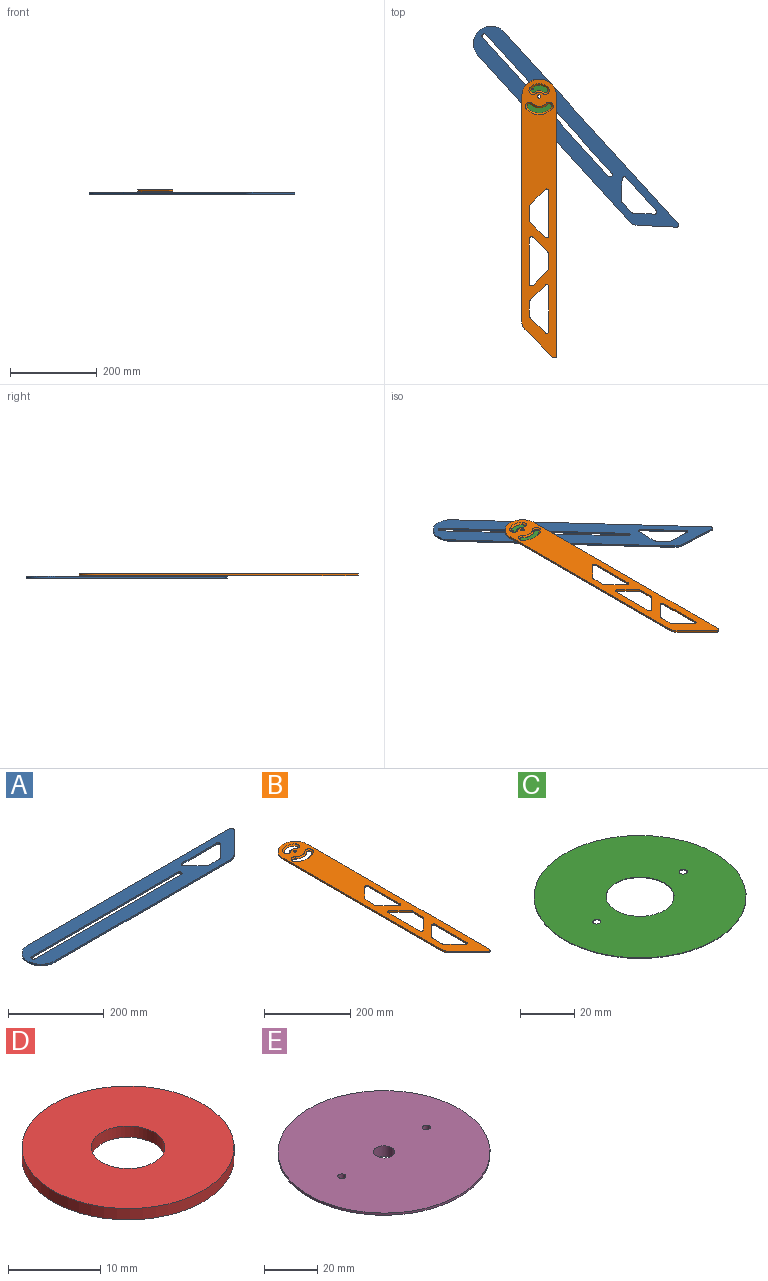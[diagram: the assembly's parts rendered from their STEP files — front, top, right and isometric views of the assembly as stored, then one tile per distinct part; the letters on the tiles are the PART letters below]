
ASSEMBLY  parts=5 mates=4
PART A: 20 faces, bbox 642.5x80x4 mm
  f0: plane 33.54x33.54mm, normal (0.71,0.71,0), area 189.7mm2, adj f14,f15,f16,f19
  f1: plane 28.72x4mm, normal (0,1,0), area 114.9mm2, adj f14,f15,f16,f17
  f2: plane 33.54x33.54mm, normal (-0.71,0.71,0), area 189.7mm2, adj f14,f15,f17,f18
  f3: cylinder r=5.25mm len=10.5mm, axis (0,0,1), area 66mm2, adj f4,f11,f14,f15
  f4: plane 431.4x4mm, normal (0,-1,0), area 1725.6mm2, adj f3,f5,f14,f15
  f5: cylinder r=5.25mm len=10.5mm, axis (0,0,1), area 66mm2, adj f4,f11,f14,f15
  f6: cylinder r=40mm len=80mm, axis (0,0,1), area 502.7mm2, adj f7,f12,f14,f15
  f7: plane 597.53x4mm, normal (0,1,0), area 2390.1mm2, adj f6,f8,f14,f15
  f8: cylinder r=5mm len=8.54mm, axis (0,0,1), area 47.1mm2, adj f7,f9,f14,f15
  f9: plane 64.14x64.14mm, normal (0.71,-0.71,0), area 362.8mm2, adj f8,f10,f14,f15
  f10: cylinder r=25mm len=17.68mm, axis (0,0,1), area 78.5mm2, adj f9,f12,f14,f15
  f11: plane 431.4x4mm, normal (0,1,0), area 1725.6mm2, adj f3,f5,f14,f15
  f12: plane 519.24x4mm, normal (0,-1,0), area 2077mm2, adj f6,f10,f14,f15
  f13: plane 102.86x4mm, normal (0,-1,0), area 411.4mm2, adj f14,f15,f18,f19
  f14: plane 642.53x80mm, normal (0,0,-1), area 39796.7mm2, adj f0,f1,f2,f3,f4,f5,f6,f7
  f15: plane 642.53x80mm, normal (0,0,1), area 39796.7mm2, adj f0,f1,f2,f3,f4,f5,f6,f7
  f16: cylinder r=10mm len=7.07mm, axis (0,0,-1), area 31.4mm2, adj f0,f1,f14,f15
  f17: cylinder r=10mm len=7.07mm, axis (0,0,-1), area 31.4mm2, adj f1,f2,f14,f15
  f18: cylinder r=5mm len=8.54mm, axis (0,0,-1), area 47.1mm2, adj f2,f13,f14,f15
  f19: cylinder r=5mm len=8.54mm, axis (0,0,-1), area 47.1mm2, adj f0,f13,f14,f15
PART B: 49 faces, bbox 80x642.5x4 mm
  f0: plane 102.86x4mm, normal (-1,0,0), area 411.4mm2, adj f19,f20,f47,f48
  f1: plane 33.54x33.54mm, normal (0.71,0.71,0), area 189.7mm2, adj f19,f20,f41,f47
  f2: plane 28.72x4mm, normal (1,0,0), area 114.9mm2, adj f19,f20,f41,f42
  f3: plane 64.14x64.14mm, normal (-0.71,-0.71,0), area 362.8mm2, adj f4,f15,f19,f20
  f4: cylinder r=5mm len=8.54mm, axis (0,0,-1), area 47.1mm2, adj f3,f5,f19,f20
  f5: plane 597.53x4mm, normal (1,0,0), area 2390.1mm2, adj f4,f6,f19,f20
  f6: cylinder r=40mm len=80mm, axis (0,0,-1), area 502.7mm2, adj f5,f7,f19,f20
  f7: plane 519.24x4mm, normal (-1,0,0), area 2077mm2, adj f6,f15,f19,f20
  f8: plane 102.86x4mm, normal (1,0,0), area 411.4mm2, adj f19,f20,f45,f46
  f9: plane 33.54x33.54mm, normal (-0.71,-0.71,0), area 189.7mm2, adj f19,f20,f39,f45
  f10: plane 28.72x4mm, normal (-1,0,0), area 114.9mm2, adj f19,f20,f39,f40
  f11: plane 102.86x4mm, normal (-1,0,0), area 411.4mm2, adj f19,f20,f43,f44
  f12: plane 33.54x33.54mm, normal (0.71,0.71,0), area 189.7mm2, adj f19,f20,f37,f43
  f13: plane 28.72x4mm, normal (1,0,0), area 114.9mm2, adj f19,f20,f37,f38
  f14: plane 33.54x33.54mm, normal (0.71,-0.71,0), area 189.7mm2, adj f19,f20,f42,f48
  f15: cylinder r=25mm len=17.68mm, axis (0,0,-1), area 78.5mm2, adj f3,f7,f19,f20
  f16: plane 33.54x33.54mm, normal (-0.71,0.71,0), area 189.7mm2, adj f19,f20,f40,f46
  f17: plane 33.54x33.54mm, normal (0.71,-0.71,0), area 189.7mm2, adj f19,f20,f38,f44
  f18: cylinder r=4mm len=8mm, axis (0,0,-1), area 100.5mm2, adj f19,f20
  f19: plane 642.53x80mm, normal (0,0,1), area 34996mm2, adj f0,f1,f2,f3,f4,f5,f6,f7
  f20: plane 642.53x80mm, normal (0,0,-1), area 35908.6mm2, adj f0,f1,f2,f3,f4,f5,f6,f7
  f21: cylinder r=13.75mm len=19.45mm, axis (0,0,1), area 10.8mm2, adj f20,f22,f24,f33
  f22: cylinder r=6mm len=10.24mm, axis (0,0,1), area 9.4mm2, adj f20,f21,f23,f34
  f23: cylinder r=25.75mm len=36.42mm, axis (0,0,1), area 20.2mm2, adj f20,f22,f24,f36
  f24: cylinder r=6mm len=10.24mm, axis (0,0,1), area 9.4mm2, adj f20,f21,f23,f35
  f25: cylinder r=38.25mm len=54.09mm, axis (0,0,1), area 30mm2, adj f20,f26,f28,f32
  f26: cylinder r=6mm len=10.24mm, axis (0,0,1), area 9.4mm2, adj f20,f25,f27,f30
  f27: cylinder r=26.25mm len=37.12mm, axis (0,0,1), area 20.6mm2, adj f20,f26,f28,f29
  f28: cylinder r=6mm len=10.24mm, axis (0,0,1), area 9.4mm2, adj f20,f25,f27,f31
  f29: cone r=26.25mm half-angle=45deg, axis (0,0,-1), area 190.5mm2, adj f19,f27,f30,f31
  f30: cone r=9.5mm half-angle=45deg, axis (0,0,1), area 120.5mm2, adj f19,f26,f29,f32
  f31: cone r=9.5mm half-angle=45deg, axis (0,0,1), area 120.5mm2, adj f19,f28,f29,f32
  f32: cone r=41.75mm half-angle=45deg, axis (0,0,1), area 311mm2, adj f19,f25,f30,f31
  f33: cone r=10.25mm half-angle=45deg, axis (0,0,-1), area 93.3mm2, adj f19,f21,f34,f35
  f34: cone r=9.5mm half-angle=45deg, axis (0,0,1), area 120.5mm2, adj f19,f22,f33,f36
  f35: cone r=9.5mm half-angle=45deg, axis (0,0,1), area 120.5mm2, adj f19,f24,f33,f36
  f36: cone r=25.75mm half-angle=45deg, axis (0,0,1), area 213.8mm2, adj f19,f23,f34,f35
  f37: cylinder r=10mm len=7.07mm, axis (0,0,1), area 31.4mm2, adj f12,f13,f19,f20
  f38: cylinder r=10mm len=7.07mm, axis (0,0,1), area 31.4mm2, adj f13,f17,f19,f20
  f39: cylinder r=10mm len=7.07mm, axis (0,0,1), area 31.4mm2, adj f9,f10,f19,f20
  f40: cylinder r=10mm len=7.07mm, axis (0,0,1), area 31.4mm2, adj f10,f16,f19,f20
  f41: cylinder r=10mm len=7.07mm, axis (0,0,1), area 31.4mm2, adj f1,f2,f19,f20
  f42: cylinder r=10mm len=7.07mm, axis (0,0,1), area 31.4mm2, adj f2,f14,f19,f20
  f43: cylinder r=5mm len=8.54mm, axis (0,0,1), area 47.1mm2, adj f11,f12,f19,f20
  f44: cylinder r=5mm len=8.54mm, axis (0,0,1), area 47.1mm2, adj f11,f17,f19,f20
  f45: cylinder r=5mm len=8.54mm, axis (0,0,1), area 47.1mm2, adj f8,f9,f19,f20
  f46: cylinder r=5mm len=8.54mm, axis (0,0,1), area 47.1mm2, adj f8,f16,f19,f20
  f47: cylinder r=5mm len=8.54mm, axis (0,0,1), area 47.1mm2, adj f0,f1,f19,f20
  f48: cylinder r=5mm len=8.54mm, axis (0,0,1), area 47.1mm2, adj f0,f14,f19,f20
PART C: 6 faces, bbox 78x78x0.3 mm
  f0: cylinder r=1.5mm len=3mm, axis (0,0,-1), area 2.4mm2, adj f4,f5
  f1: cylinder r=1.5mm len=3mm, axis (0,0,-1), area 2.4mm2, adj f4,f5
  f2: cylinder r=12.5mm len=25mm, axis (0,0,-1), area 19.6mm2, adj f4,f5
  f3: cylinder r=39mm len=78mm, axis (0,0,-1), area 61.3mm2, adj f4,f5
  f4: plane 78x78mm, normal (0,0,1), area 4273.4mm2, adj f0,f1,f2,f3
  f5: plane 78x78mm, normal (0,0,-1), area 4273.4mm2, adj f0,f1,f2,f3
PART D: 4 faces, bbox 23x23x1.5 mm
  f0: cylinder r=4mm len=8mm, axis (0,0,-1), area 37.7mm2, adj f2,f3
  f1: cylinder r=11.5mm len=23mm, axis (0,0,-1), area 108.4mm2, adj f2,f3
  f2: plane 23x23mm, normal (0,0,1), area 365.2mm2, adj f0,f1
  f3: plane 23x23mm, normal (0,0,-1), area 365.2mm2, adj f0,f1
PART E: 11 faces, bbox 80x80x5 mm
  f0: cylinder r=40mm len=80mm, axis (0,0,1), area 251.3mm2, adj f1,f2
  f1: plane 80x80mm, normal (0,0,-1), area 4498mm2, adj f0,f3,f4,f5,f6
  f2: plane 80x80mm, normal (0,0,1), area 4962.1mm2, adj f0,f7,f8,f9
  f3: plane 45x4mm, normal (0,1,0), area 180mm2, adj f1,f5,f6,f10
  f4: plane 45x4mm, normal (0,-1,0), area 180mm2, adj f1,f5,f6,f10
  f5: cylinder r=5mm len=10mm, axis (0,0,1), area 62.8mm2, adj f1,f3,f4,f10
  f6: cylinder r=5mm len=10mm, axis (0,0,1), area 62.8mm2, adj f1,f3,f4,f10
  f7: cylinder r=1.5mm len=5mm, axis (0,0,1), area 47.1mm2, adj f2,f10
  f8: cylinder r=1.5mm len=5mm, axis (0,0,1), area 47.1mm2, adj f2,f10
  f9: cylinder r=4mm len=8mm, axis (0,0,1), area 125.7mm2, adj f2,f10
  f10: plane 55x10mm, normal (0,0,-1), area 464.1mm2, adj f3,f4,f5,f6,f7,f8,f9
PLACE A rot(axis=(0,0,-1),47.7deg) t=(-111.65,122.37,0)mm
PLACE B at identity fixed
PLACE C rot(axis=(0,0,-1),47.7deg) t=(0,0,0)mm
PLACE D rot(axis=(0,0,-1),47.7deg) t=(0,0,0)mm
PLACE E rot(axis=(0,0,-1),47.7deg) t=(0,0,0)mm
MATE fastened E.f0 <-> C.f2  axis (0,0,1) through (0,0,0)mm
MATE fastened D.f0 <-> E.f9  axis (0,0,-1) through (0,0,0)mm
MATE revolute C.f2 <-> B.f18  axis (0,0,1) through (0,0,0.25)mm
MATE parallel A.f4 <-> E.f3  axis (-0.74,-0.67,0) through (22.24,-17.01,-3)mm
